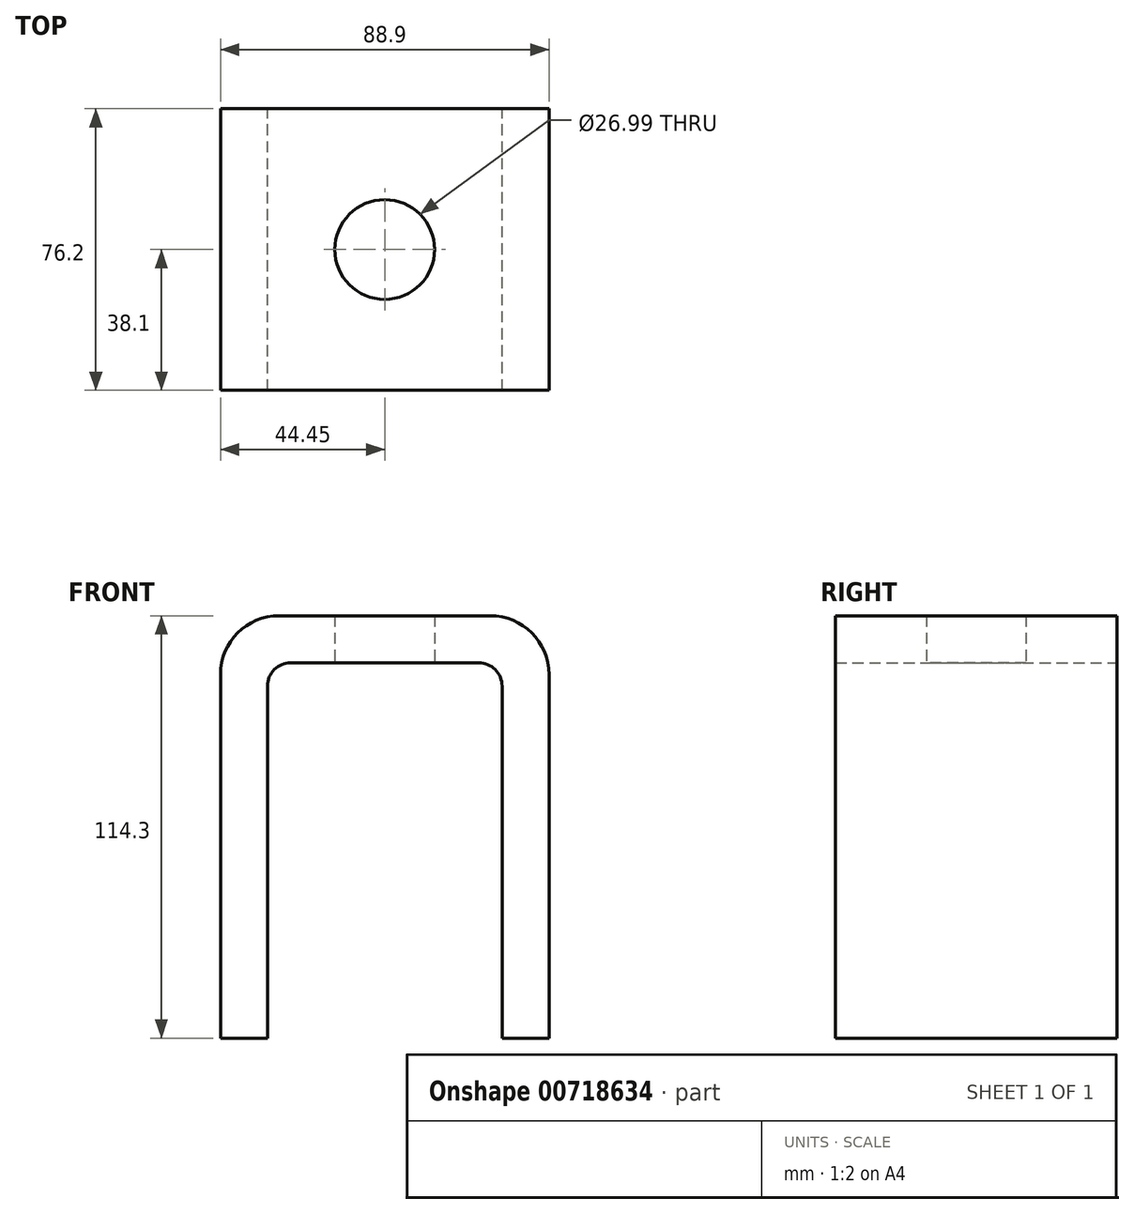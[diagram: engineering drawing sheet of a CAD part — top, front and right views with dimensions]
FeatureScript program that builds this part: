
annotation { "Feature Type Name" : "Feature", "Feature Type Description" : "" }
export const myFeature = defineFeature(function(context is Context, id is Id, definition is map)
    precondition{}
    {
        {
            var Q0;
            Q0=qCreatedBy(makeId("Front.planeOp"),FACE);
            var sketch = newSketch(context, id + "F0", { "sketchPlane" : qUnion([Q0])});
            skLineSegment(sketch, "E0.bottom", {"start": v(44.45, -57.15) * mm, "end": v(31.75, -57.15) * mm});
            skLineSegment(sketch, "E0.top", {"start": v(44.45, 57.15) * mm, "end": v(-44.45, 57.15) * mm});
            skLineSegment(sketch, "E0.left", {"start": v(44.45, -57.15) * mm, "end": v(44.45, 57.15) * mm});
            skLineSegment(sketch, "E0.right", {"start": v(-44.45, -57.15) * mm, "end": v(-44.45, 57.15) * mm});
            skPoint(sketch, "E0.middle", {"position": v(0, 0) * mm});
            skLineSegment(sketch, "E1.0", {"start": v(-31.75, -57.15) * mm, "end": v(-31.75, 44.45) * mm});
            skLineSegment(sketch, "E2.0", {"start": v(31.75, 44.45) * mm, "end": v(-31.75, 44.45) * mm});
            skLineSegment(sketch, "E3.0", {"start": v(31.75, -57.15) * mm, "end": v(31.75, 44.45) * mm});
            skLineSegment(sketch, "E4.trimOffspring", {"start": v(-31.75, -57.15) * mm, "end": v(-44.45, -57.15) * mm});
            skSolve(sketch);
        }
        {
            var Q0;
            Q0 = qSketchRegion(id + "F0", true);
            extrude(context, id + "F1", {"entities" : qUnion([Q0]), "depth" : 76.2 * mm, "offsetDistance" : 25.4 * mm, "symmetric" : true});
        }
        {
            var Q0;
            Q0=makeQuery(id+"F1.opExtrude","SWEPT_EDGE",EDGE,{"disambiguationData":[OSD([sQuery(id+"F0.wireOp",EDGE,"E1.0"),sQuery(id+"F0.wireOp",EDGE,"E2.0")])]});
            var Q1;
            Q1=makeQuery(id+"F1.opExtrude","SWEPT_EDGE",EDGE,{"disambiguationData":[OSD([sQuery(id+"F0.wireOp",EDGE,"E2.0"),sQuery(id+"F0.wireOp",EDGE,"E3.0")])]});
            fillet(context, id + "F2", {"entities" : qUnion([Q0, Q1]), "radius" : 6.35 * mm, "tangentPropagation" : true, "allowEdgeOverflow" : false});
        }
        {
            var Q0;
            Q0=makeQuery(id+"F1.opExtrude","SWEPT_EDGE",EDGE,{"disambiguationData":[OSD([sQuery(id+"F0.wireOp",EDGE,"E0.top"),sQuery(id+"F0.wireOp",EDGE,"E0.right")])]});
            var Q1;
            Q1=makeQuery(id+"F1.opExtrude","SWEPT_EDGE",EDGE,{"disambiguationData":[OSD([sQuery(id+"F0.wireOp",EDGE,"E0.top"),sQuery(id+"F0.wireOp",EDGE,"E0.left")])]});
            fillet(context, id + "F3", {"entities" : qUnion([Q0, Q1]), "radius" : 15.88 * mm, "tangentPropagation" : true, "allowEdgeOverflow" : false});
        }
        {
            var Q0;
            Q0=qCreatedBy(makeId("Top.planeOp"),FACE);
            var sketch = newSketch(context, id + "F4", { "sketchPlane" : qUnion([Q0])});
            skCircle(sketch, "E5", {"center": v(0, 0) * mm, "radius": 13.5 * mm});
            skSolve(sketch);
        }
        {
            var Q0;
            Q0 = qSketchRegion(id + "F4", true);
            extrude(context, id + "F5", {"entities" : qUnion([Q0]), "operationType" : NewBodyOperationType.REMOVE, "endBound" : BoundingType.THROUGH_ALL, "depth" : 25.4 * mm, "offsetDistance" : 25.4 * mm});
        }
    });
